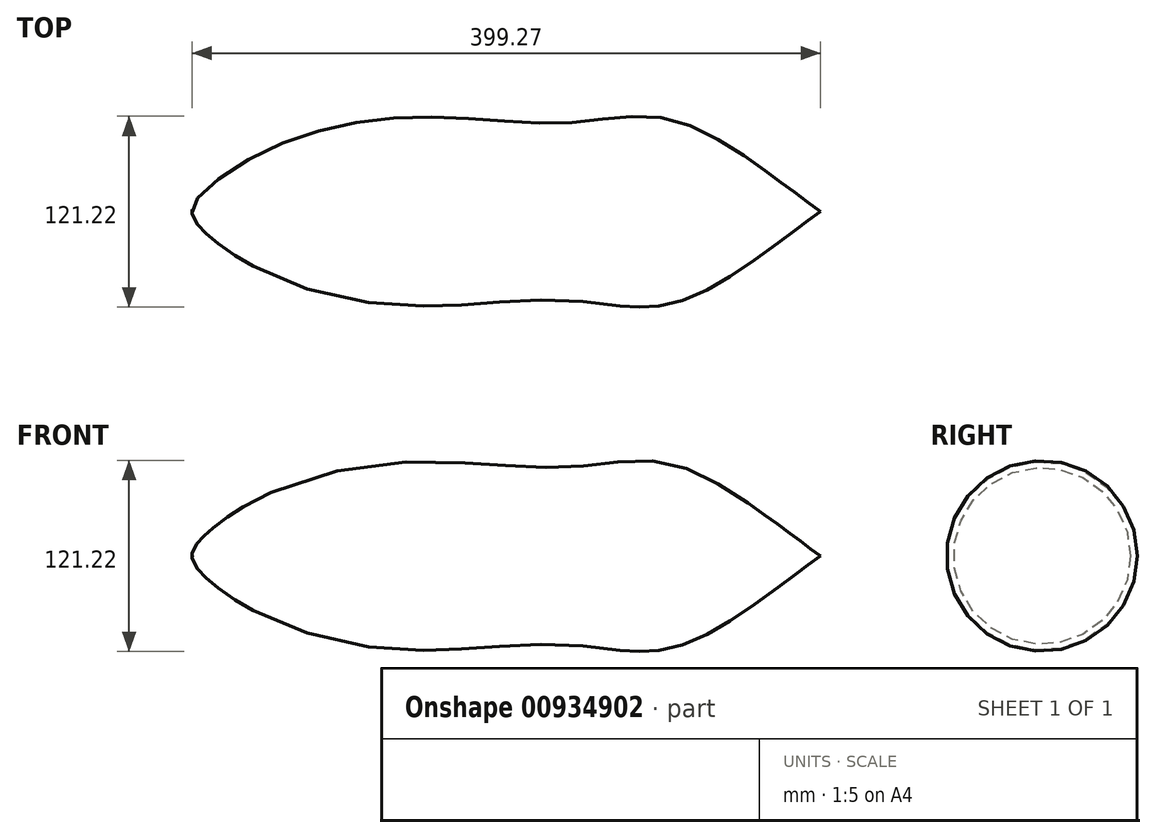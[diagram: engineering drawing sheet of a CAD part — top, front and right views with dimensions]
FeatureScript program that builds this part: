
annotation { "Feature Type Name" : "Feature", "Feature Type Description" : "" }
export const myFeature = defineFeature(function(context is Context, id is Id, definition is map)
    precondition{}
    {
        {
            var Q0;
            Q0=qCreatedBy(makeId("Top.planeOp"),FACE);
            var sketch = newSketch(context, id + "F0", { "sketchPlane" : qUnion([Q0])});
            skLineSegment(sketch, "E0", {"start": v(0, 0) * mm, "end": v(-398.92, 0) * mm});
            skFitSpline(sketch, "E1", {"points": [v(-398.92, 0) * mm, v(-361.73, 33.93) * mm, v(-257.89, 59.9) * mm, v(-162.18, 56.38) * mm, v(-95.44, 58.64) * mm, v(-37.08, 27.15) * mm, v(-16.35, 11.95) * mm, v(0, 0) * mm], "startDerivative": vector(-70.2, 131.02) * mm, "endDerivative": vector(186.74, -123.64) * mm});
            skSolve(sketch);
        }
        {
            var Q0;
            Q0=makeQuery(id+"F0.imprint","IMPRINT",FACE,{"disambiguationData":[TD([[makeQuery(id+"F0.imprint","IMPRINT",EDGE,{"derivedFrom":sQuery(id+"F0.wireOp",EDGE,"E0")}),-1.0]])]});
            var Q1;
            Q1=sQuery(id+"F0.wireOp",EDGE,"E0");
            revolve(context, id + "F1", {"surfaceOperationType" : NewSurfaceOperationType.NEW, "entities" : qUnion([Q0]), "axis" : qUnion([Q1]), "revolveType" : RevolveType.FULL});
        }
    });
